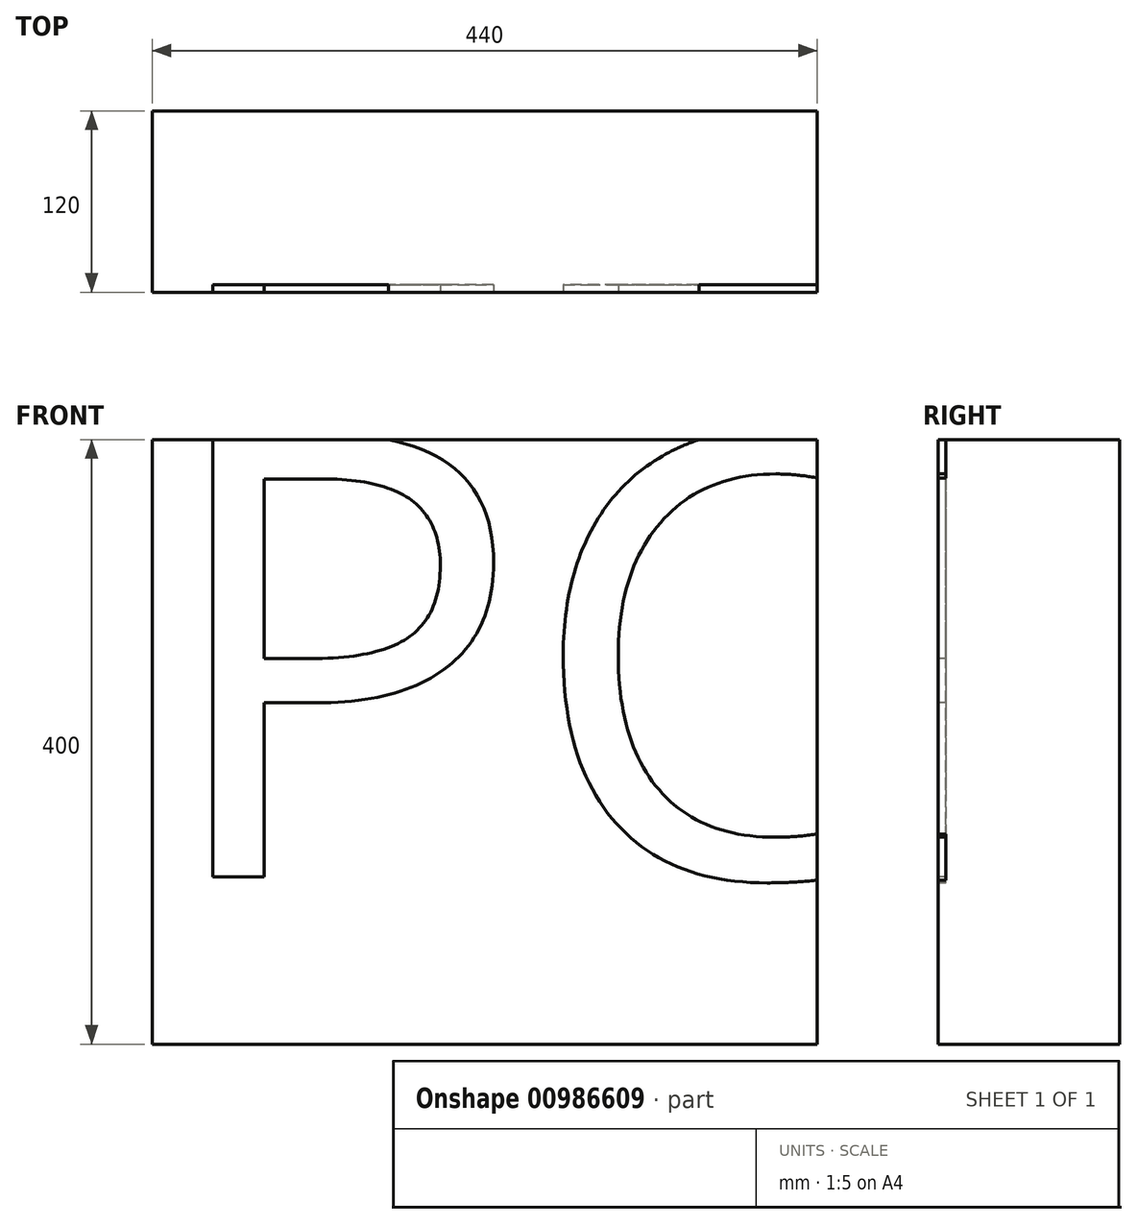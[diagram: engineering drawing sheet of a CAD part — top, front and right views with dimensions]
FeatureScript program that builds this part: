
annotation { "Feature Type Name" : "Feature", "Feature Type Description" : "" }
export const myFeature = defineFeature(function(context is Context, id is Id, definition is map)
    precondition{}
    {
        {
            var Q0;
            Q0=qCreatedBy(makeId("Right.planeOp"),FACE);
            var sketch = newSketch(context, id + "F0", { "sketchPlane" : qUnion([Q0])});
            skLineSegment(sketch, "E0.bottom", {"start": v(39.1, 40.85) * mm, "end": v(159.1, 40.85) * mm});
            skLineSegment(sketch, "E0.top", {"start": v(39.1, 440.85) * mm, "end": v(159.1, 440.85) * mm});
            skLineSegment(sketch, "E0.left", {"start": v(39.1, 40.85) * mm, "end": v(39.1, 440.85) * mm});
            skLineSegment(sketch, "E0.right", {"start": v(159.1, 40.85) * mm, "end": v(159.1, 440.85) * mm});
            skSolve(sketch);
        }
        {
            var Q0;
            Q0=makeQuery(id+"F0.imprint","IMPRINT",FACE,{"disambiguationData":[TD([[makeQuery(id+"F0.imprint","IMPRINT",EDGE,{"derivedFrom":sQuery(id+"F0.wireOp",EDGE,"E0.bottom")}),1.0]])]});
            extrude(context, id + "F1", {"entities" : qUnion([Q0]), "depth" : 440 * mm, "offsetDistance" : 25 * mm});
        }
        {
            var Q0;
            Q0=makeQuery(id+"F1.opExtrude","SWEPT_FACE",FACE,{"disambiguationData":[OSD([sQuery(id+"F0.wireOp",EDGE,"E0.left")])]});
            var sketch = newSketch(context, id + "F2", { "sketchPlane" : qUnion([Q0])});
            skText(sketch, "E1", { "text": "PC", "fontName": "OpenSans-Regular.ttf"});
            const initialGuessF2  = {"E1": [0, 0.15159, 1, 0, 0.29528]};
            skSetInitialGuess(sketch, initialGuessF2);
            skSolve(sketch);
        }
        {
            var Q0;
            Q0=qSketchRegion(id+"F2",true);
            extrude(context, id + "F3", {"entities" : qUnion([Q0]), "operationType" : NewBodyOperationType.REMOVE, "oppositeDirection" : true, "depth" : 5 * mm, "offsetDistance" : 25 * mm});
        }
    });
